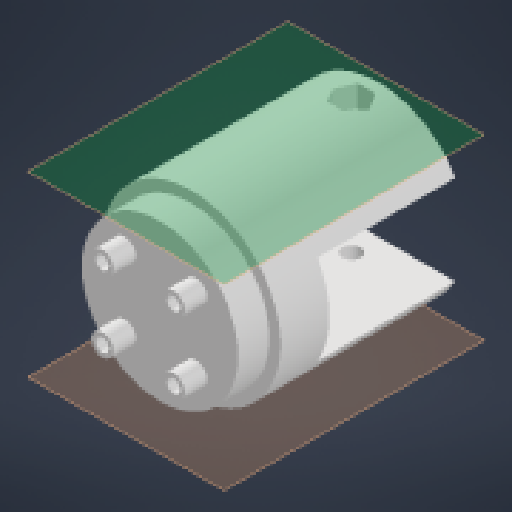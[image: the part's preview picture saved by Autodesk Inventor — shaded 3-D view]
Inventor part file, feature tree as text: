
AUTODESK INVENTOR PART (.ipt)
format: ipt  version: 2023.2 (Build 272271000, 271)  size: 239,104 bytes
history: native  units: mm
features: extrude x9, sketch x6, reference x3, other x3, plane x2, thicken_offset x2, pattern_circular x1, projected_geometry x1
ambient origin geometry x8: Origin, YZ Plane, XZ Plane, XY Plane, X Axis, Y Axis, Z Axis, Center Point
bodies: Solid1 (feature_tree)
feature tree (27):
  sketch  "Sketch1"  dims[d0=40.0mm d1=11.0mm d2=0.0mm]
  extrude  "Extrusion1"  Depth=11.0mm TaperAngle=0.0deg
  extrude  "Extrusion2"  Depth=35.0mm
  sketch  "Sketch2"  dims[d3=30.0mm d4=0.0mm d5=35.0mm]
  extrude  "Extrusion3"  Depth=16.0mm
  extrude  "Extrusion4"  Depth=5.0mm
  extrude  "Extrusion5"  Depth=2.0mm TaperAngle=0.0deg
  extrude  "Extrusion6"  Depth=5.0mm TaperAngle=0.0deg
  pattern_circular  "Circular Pattern1"  [2 undecoded]
  extrude  "Extrusion7"  Depth=20.0mm TaperAngle=360.0deg
  plane  "Work Plane1"
  extrude  "Extrusion8"  Depth=5.0mm
  plane  "Work Plane2"
  extrude  "Extrusion9"  TaperAngle=0.0deg  [1 undecoded]
  thicken_offset  "Thicken1"
  thicken_offset  "Thicken2"
  reference  "Reference1"
  reference  "Reference2"
  sketch  "Sketch3"  dims[d6=16.0mm d7=16.0mm]
  projected_geometry  "Projected Loop1"
  sketch  "Sketch4"  dims[d8=3.0mm d9=5.0mm]
  reference  "Reference3"
  sketch  "Sketch5"  dims[d10=40.0mm d12=360.0deg d14=2.0mm d15=0.0mm]
  sketch  "Sketch6"  dims[d16=7.0mm d17=0.0mm d18=12.0mm d19=0.0mm d20=0.07mm d21=0.0mm d22=20.0mm d23=360.0deg d25=4.0mm d26=0.0mm d27=0.0mm d28=10.0mm d29=5.0mm d30=0.0mm d31=7.0mm d32=5.0mm d33=0.0mm d34=1.0mm d35=1.0mm d36=1.0mm d37=1.0mm]
  parser-record x1  (decoder bookkeeping rows leaked as tree rows — omitted from the tree; the rows remain in map.json)
  other  "turret_assembly.iam"
  other  "pylon:3"
note: 3 required parameter values undecoded (feature->parameter linkage not recoverable at this tier; creation-order binding heuristic only, values carry confidence <= 0.55)
note: 1 file-system path scrubbed to <path> (originals preserved in map.json)
